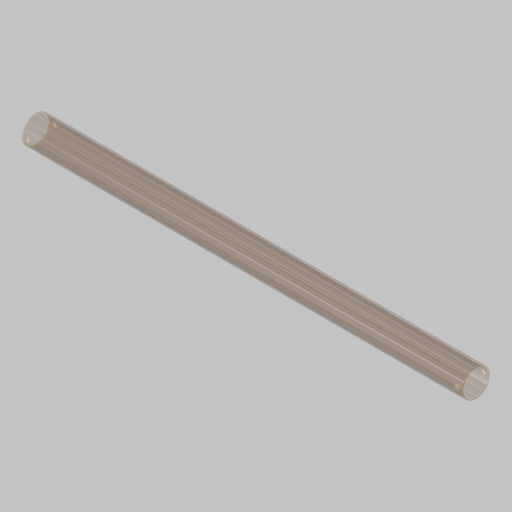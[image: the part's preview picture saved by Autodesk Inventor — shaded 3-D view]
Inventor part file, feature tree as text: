
AUTODESK INVENTOR PART (.ipt)
format: ipt  version: 2023.5 (Build 275446000, 446)  size: 128,512 bytes
history: native  units: in
note: dims shown in document units (in); Inventor stores cm internally (conversion verified against a paired STEP export)
features: sketch x2, extrude x1, plane x1, hole x1
ambient origin geometry x8: Origin, YZ Plane, XZ Plane, XY Plane, X Axis, Y Axis, Z Axis, Center Point
bodies: Solid1 (feature_tree)
feature tree (5):
  extrude  "Extrusion1"  Depth=0.0625in
  plane  "Work Plane1"
  hole  "Hole2"  [1 undecoded]
  sketch  "Sketch1"  dims[d0=1.25in d2=0.0625in]
  sketch  "Sketch3"  dims[d3=19.75in d4=0.0in d14=0.6875in d15=0.25in d16=0.25in d17=0.201in d18=0.75in d19=0.375in d20=0.25in d21=0.5635in d22=1.0in d23=0.8108in]
note: 1 required parameter value undecoded (feature->parameter linkage not recoverable at this tier; creation-order binding heuristic only, values carry confidence <= 0.55)
